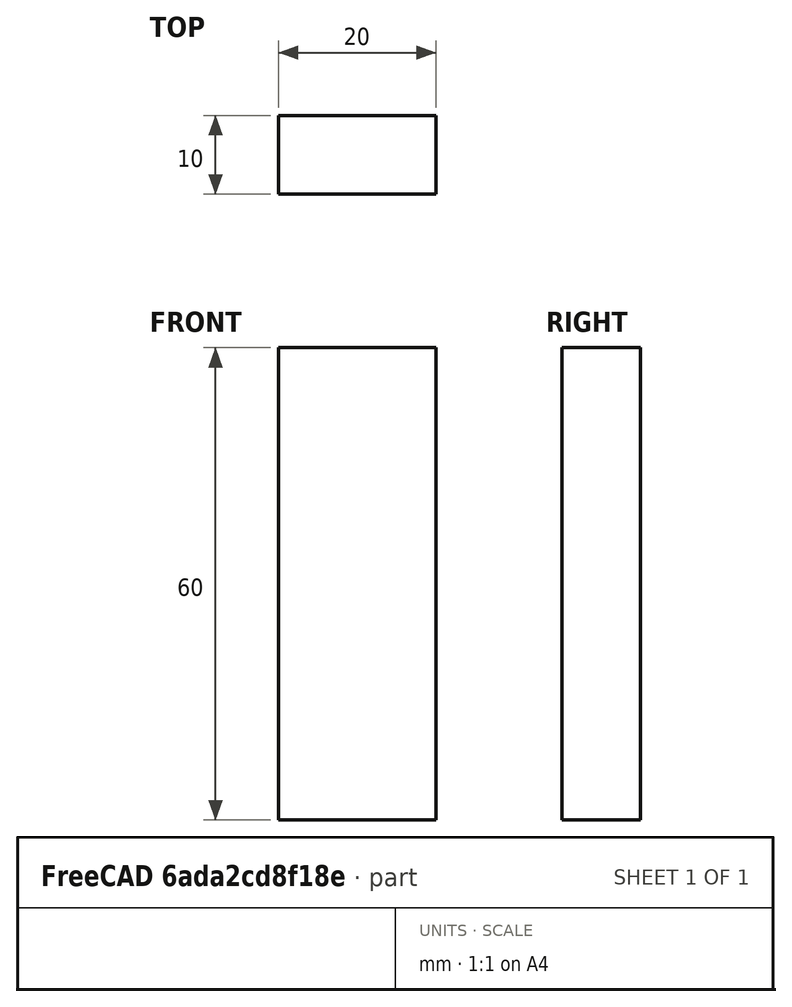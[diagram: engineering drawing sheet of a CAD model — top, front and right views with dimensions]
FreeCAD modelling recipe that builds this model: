
FCSTD DOCUMENT  (FreeCAD 1.0R39109 (Git))
Label: parametric_prism
License: All rights reserved
LicenseURL: https://en.wikipedia.org/wiki/All_rights_reserved
objects: Sketcher::SketchObject×1, Spreadsheet::Sheet×1, PartDesign::Pad×1, PartDesign::Body×1
note: 6 computed .brp shape members not serialized (recipe doc carries the construction recipe); baked Part::Feature solids carry a one-line shape summary decoded from their .brp

FEATURE [Sketcher::SketchObject] Sketch
  ArcFitTolerance = 1e-06
  AttachmentSupport = -> [XY_Plane]
  FullyConstrained = true
  MakeInternals = false
  MapMode = 5
  expr: Constraints[10] = Spreadsheet.dim_Y
  expr: Constraints[9] = Spreadsheet.dim_X
  sketch-geometry (4):
    g0: LineSegment StartX=-10 StartY=5 StartZ=0 EndX=-10 EndY=-5 EndZ=0
    g1: LineSegment StartX=-10 StartY=-5 StartZ=0 EndX=10 EndY=-5 EndZ=0
    g2: LineSegment StartX=10 StartY=-5 StartZ=0 EndX=10 EndY=5 EndZ=0
    g3: LineSegment StartX=10 StartY=5 StartZ=0 EndX=-10 EndY=5 EndZ=0
  constraints (11):
    c: Coincident(g0,g1)
    c: Coincident(g1,g2)
    c: Coincident(g2,g3)
    c: Coincident(g3,g0)
    c: Vertical(g0)
    c: Vertical(g2)
    c: Horizontal(g1)
    c: Horizontal(g3)
    c: Symmetric(g0,g2,g-1)
    c: DistanceX(g1,g1) = 20
    c: DistanceY(g2,g2) = 10
FEATURE [Spreadsheet::Sheet] Spreadsheet
  cells = A1='X; B1(dim_X)=20; A2='Y; B2(dim_Y)=10; A3='Z; B3(dim_Z)=60
FEATURE [PartDesign::Pad] Pad  label="prism"
  Direction = (0,0,1)
  Length = 60
  Length2 = 10
  Profile = -> Sketch
  ReferenceAxis = -> Sketch [N_Axis]
  Refine = true
  Suppressed = false
  Type = 0
  expr: Length = Spreadsheet.dim_Z
FEATURE [PartDesign::Body] Body
  AllowCompound = false
  Group = -> [Sketch,Pad]
  Origin = -> Origin
  Tip = -> Pad
